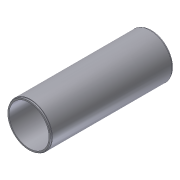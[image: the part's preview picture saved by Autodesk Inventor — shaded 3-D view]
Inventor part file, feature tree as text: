
AUTODESK INVENTOR PART (.ipt)
format: ipt  version: 2013 (Build 170138000, 138)  size: 89,088 bytes
history: native  units: in
note: dims shown in document units (in); Inventor stores cm internally (conversion verified against a paired STEP export)
features: sketch x2, extrude x1, revolve x1, mirror x1
ambient origin geometry x8: Origin, YZ Plane, XZ Plane, XY Plane, X Axis, Y Axis, Z Axis, Center Point
bodies: Solid1 (feature_tree)
feature tree (5):
  extrude  "Extrusion1"  Depth=0.1in
  revolve  "Revolution1"  [1 undecoded]
  mirror  "Mirror1"
  sketch  "Sketch1"  dims[d0=2.062in d1=0.1in]
  sketch  "Sketch2"  dims[d2=5.72in d3=0.0in d4=0.0625in d5=0.031in d6=90.0deg]
note: 1 required parameter value undecoded (feature->parameter linkage not recoverable at this tier; creation-order binding heuristic only, values carry confidence <= 0.55)
